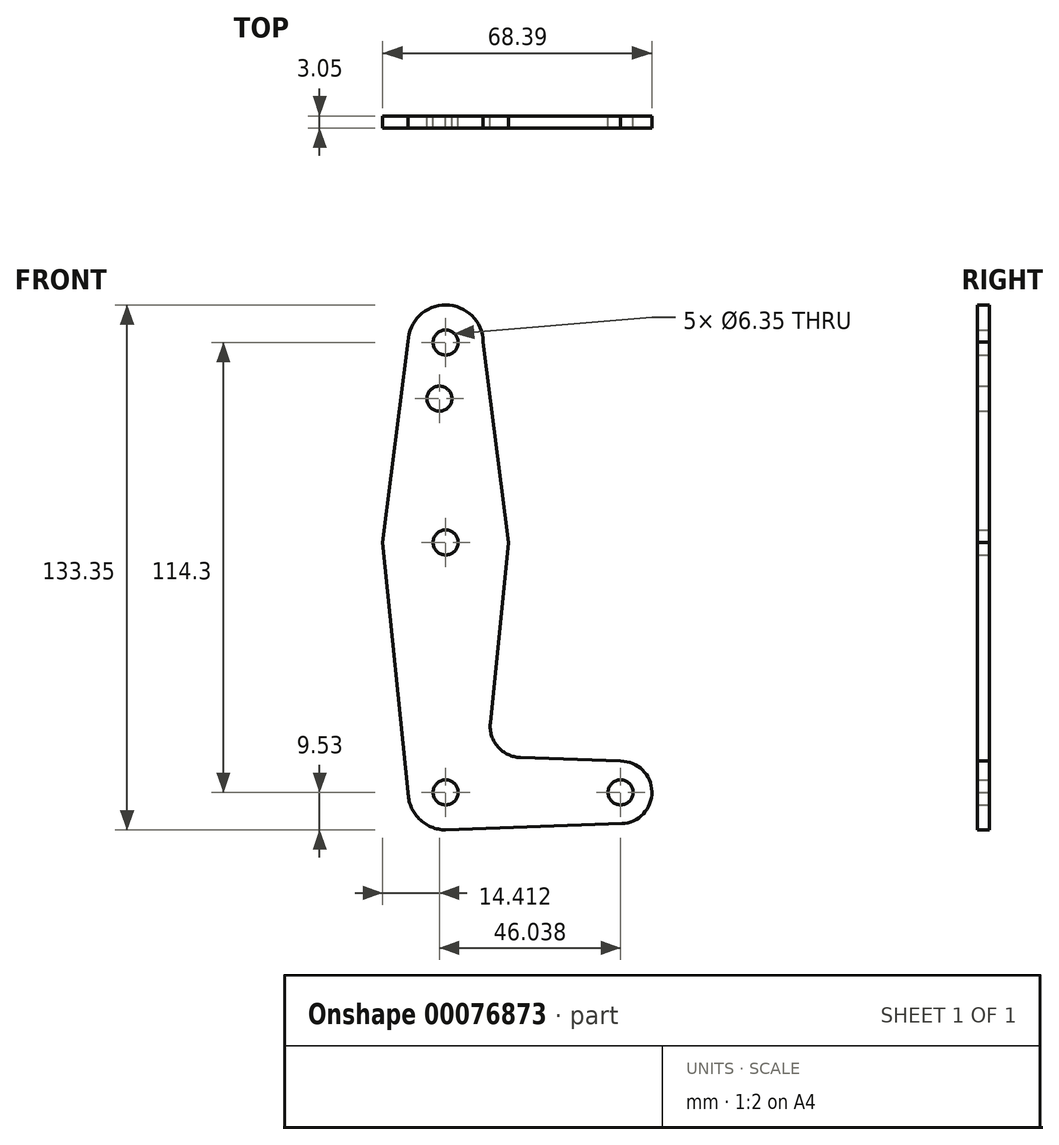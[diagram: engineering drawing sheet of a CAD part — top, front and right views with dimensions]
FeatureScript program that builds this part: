
annotation { "Feature Type Name" : "Feature", "Feature Type Description" : "" }
export const myFeature = defineFeature(function(context is Context, id is Id, definition is map)
    precondition{}
    {
        {
            var Q0;
            Q0=qCreatedBy(makeId("Front.planeOp"),FACE);
            var sketch = newSketch(context, id + "F0", { "sketchPlane" : qUnion([Q0])});
            skCircle(sketch, "E0", {"center": v(0, 0) * mm, "radius": 15.88 * mm});
            skLineSegment(sketch, "E1", {"start": v(0, 50.8) * mm, "end": v(0, -63.5) * mm, "construction": true});
            skLineSegment(sketch, "E2", {"start": v(0, -63.5) * mm, "end": v(44.45, -63.5) * mm});
            skCircle(sketch, "E3", {"center": v(0, 50.8) * mm, "radius": 9.53 * mm});
            skCircle(sketch, "E4", {"center": v(0, -63.5) * mm, "radius": 9.53 * mm});
            skCircle(sketch, "E5", {"center": v(44.45, -63.5) * mm, "radius": 7.94 * mm});
            skLineSegment(sketch, "E6", {"start": v(-9.52, 51.06) * mm, "end": v(-16, 0) * mm});
            skLineSegment(sketch, "E7", {"start": v(9.52, 50.98) * mm, "end": v(16, 0) * mm});
            skLineSegment(sketch, "E8", {"start": v(16, 0) * mm, "end": v(11.35, -45.9) * mm});
            skLineSegment(sketch, "E9", {"start": v(-16, 0) * mm, "end": v(-9.52, -63.45) * mm});
            skLineSegment(sketch, "E10", {"start": v(0, -73.03) * mm, "end": v(44.73, -71.43) * mm});
            skLineSegment(sketch, "E11", {"start": v(18.98, -54.65) * mm, "end": v(44.45, -55.56) * mm});
            skArc(sketch, "E12.filletArc", {"start": v(11.35, -45.9) * mm, "mid": v(13.27, -51.93) * mm, "end": v(18.98, -54.65) * mm});
            skCircle(sketch, "E13", {"center": v(0, 50.8) * mm, "radius": 3.18 * mm});
            skCircle(sketch, "E14", {"center": v(0, 0) * mm, "radius": 3.18 * mm});
            skCircle(sketch, "E15", {"center": v(0, -63.5) * mm, "radius": 3.18 * mm});
            skCircle(sketch, "E16", {"center": v(44.45, -63.5) * mm, "radius": 3.18 * mm});
            skCircle(sketch, "E17", {"center": v(-1.59, 36.53) * mm, "radius": 3.18 * mm});
            skSolve(sketch);
        }
        {
            var Q0;
            Q0=qCreatedBy(makeId("Front.planeOp"),FACE);
            var sketch = newSketch(context, id + "F1", { "sketchPlane" : qUnion([Q0])});
            skSolve(sketch);
        }
        {
            var Q0;
            Q0 = qSketchRegion(id + "F1", true);
            var Q1;
            Q1=makeQuery(id+"F0.imprint","IMPRINT",FACE,{"disambiguationData":[TD([[makeQuery(id+"F0.imprint","IMPRINT",EDGE,{"derivedFrom":sQuery(id+"F0.wireOp",EDGE,"E17")}),-1.0]])]});
            var Q2;
            Q2=makeQuery(id+"F0.imprint","IMPRINT",FACE,{"disambiguationData":[TD([[makeQuery(id+"F0.imprint","IMPRINT",EDGE,{"derivedFrom":sQuery(id+"F0.wireOp",EDGE,"E14")}),-1.0]])]});
            var Q3;
            {var subQ12=sQuery(id+"F0.wireOp",EDGE,"E8");Q3=makeQuery(id+"F0.imprint","IMPRINT",FACE,{"disambiguationData":[TD([[makeQuery(id+"F0.imprint","IMPRINT",EDGE,{"derivedFrom":subQ12}),-1.0]])]});}
            var Q4;
            Q4=makeQuery(id+"F0.imprint","IMPRINT",FACE,{"disambiguationData":[TD([[makeQuery(id+"F0.imprint","IMPRINT",EDGE,{"derivedFrom":sQuery(id+"F0.wireOp",EDGE,"E13")}),-1.0]])]});
            var Q5;
            {var subQ0=sQuery(id+"F0.wireOp",EDGE,"E4");var subQ1=sQuery(id+"F0.wireOp",EDGE,"E2");var subQ2=makeQuery(id+"F0.imprint","INTERSECT",VERTEX,{"derivedFrom":[subQ1,subQ0]});Q5=makeQuery(id+"F0.imprint","IMPRINT",FACE,{"disambiguationData":[TD([[makeQuery(id+"F0.imprint","IMPRINT",EDGE,{"disambiguationData":[TD([[subQ2,-1.0]])],"derivedFrom":subQ1}),-1.0]])]});}
            var Q6;
            Q6=makeQuery(id+"F0.imprint","IMPRINT",FACE,{"disambiguationData":[TD([[makeQuery(id+"F0.imprint","IMPRINT",EDGE,{"derivedFrom":sQuery(id+"F0.wireOp",EDGE,"E16")}),-1.0]])]});
            var Q7;
            Q7=makeQuery(id+"F0.imprint","IMPRINT",FACE,{"disambiguationData":[TD([[makeQuery(id+"F0.imprint","IMPRINT",EDGE,{"derivedFrom":sQuery(id+"F0.wireOp",EDGE,"E15")}),-1.0]])]});
            var Q8;
            {var subQ0=sQuery(id+"F0.wireOp",EDGE,"E10");var subQ1=sQuery(id+"F0.wireOp",EDGE,"E4");var subQ2=makeQuery(id+"F0.imprint","INTERSECT",VERTEX,{"disambiguationData":[OD(0.0)],"derivedFrom":[subQ1,subQ0]});Q8=makeQuery(id+"F0.imprint","IMPRINT",FACE,{"disambiguationData":[TD([[makeQuery(id+"F0.imprint","IMPRINT",EDGE,{"disambiguationData":[TD([[subQ2,-1.0]])],"derivedFrom":subQ1}),1.0]])]});}
            extrude(context, id + "F2", {"entities" : qUnion([Q0, Q1, Q2, Q3, Q4, Q5, Q6, Q7, Q8]), "depth" : 3.05 * mm});
        }
    });
